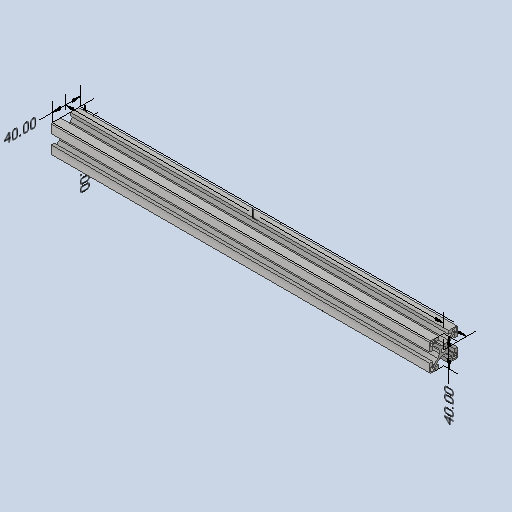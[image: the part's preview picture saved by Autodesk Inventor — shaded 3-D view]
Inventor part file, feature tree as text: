
AUTODESK INVENTOR PART (.ipt)
format: ipt  version: 2023 (Build 270158000, 158)  size: 276,480 bytes
history: native  units: mm
features: other x125, extrude x1, sketch x1
ambient origin geometry x8: Origin, YZ Plane, XZ Plane, XY Plane, X Axis, Y Axis, Z Axis, Center Point
bodies: Solid1 (feature_tree)
feature tree (127):
  other  "Annotations"
  extrude  "Extrusion1"  [1 undecoded]
  other  "CS_ANBAU_HINTEN_LINKS_XY"
  other  "CS_ANBAU_HINTEN_LINKS_YZ"
  other  "CS_ANBAU_HINTEN_LINKS_ZX"
  other  "CS_ANBAU_HINTEN_LINKS_X"
  other  "CS_ANBAU_HINTEN_LINKS_Y"
  other  "CS_ANBAU_HINTEN_LINKS_Z"
  other  "CS_ANBAU_HINTEN_LINKS_Center"
  other  "CS_ANBAU_HINTEN_OBEN_XY"
  other  "CS_ANBAU_HINTEN_OBEN_YZ"
  other  "CS_ANBAU_HINTEN_OBEN_ZX"
  other  "CS_ANBAU_HINTEN_OBEN_X"
  other  "CS_ANBAU_HINTEN_OBEN_Y"
  other  "CS_ANBAU_HINTEN_OBEN_Z"
  other  "CS_ANBAU_HINTEN_OBEN_Center"
  other  "CS_ANBAU_HINTEN_RECHTS_XY"
  other  "CS_ANBAU_HINTEN_RECHTS_YZ"
  other  "CS_ANBAU_HINTEN_RECHTS_ZX"
  other  "CS_ANBAU_HINTEN_RECHTS_X"
  other  "CS_ANBAU_HINTEN_RECHTS_Y"
  other  "CS_ANBAU_HINTEN_RECHTS_Z"
  other  "CS_ANBAU_HINTEN_RECHTS_Center"
  other  "CS_ANBAU_HINTEN_UNTEN_XY"
  other  "CS_ANBAU_HINTEN_UNTEN_YZ"
  other  "CS_ANBAU_HINTEN_UNTEN_ZX"
  other  "CS_ANBAU_HINTEN_UNTEN_X"
  other  "CS_ANBAU_HINTEN_UNTEN_Y"
  other  "CS_ANBAU_HINTEN_UNTEN_Z"
  other  "CS_ANBAU_HINTEN_UNTEN_Center"
  other  "CS_ANBAU_QUER_XY"
  other  "CS_ANBAU_QUER_YZ"
  other  "CS_ANBAU_QUER_ZX"
  other  "CS_ANBAU_QUER_X"
  other  "CS_ANBAU_QUER_Y"
  other  "CS_ANBAU_QUER_Z"
  other  "CS_ANBAU_QUER_Center"
  other  "CS_ANBAU_QUER_1_XY"
  other  "CS_ANBAU_QUER_1_YZ"
  other  "CS_ANBAU_QUER_1_ZX"
  other  "CS_ANBAU_QUER_1_X"
  other  "CS_ANBAU_QUER_1_Y"
  other  "CS_ANBAU_QUER_1_Z"
  other  "CS_ANBAU_QUER_1_Center"
  other  "CS_ANBAU_VORNE_LINKS_XY"
  other  "CS_ANBAU_VORNE_LINKS_YZ"
  other  "CS_ANBAU_VORNE_LINKS_ZX"
  other  "CS_ANBAU_VORNE_LINKS_X"
  other  "CS_ANBAU_VORNE_LINKS_Y"
  other  "CS_ANBAU_VORNE_LINKS_Z"
  other  "CS_ANBAU_VORNE_LINKS_Center"
  other  "CS_ANBAU_VORNE_OBEN_XY"
  other  "CS_ANBAU_VORNE_OBEN_YZ"
  other  "CS_ANBAU_VORNE_OBEN_ZX"
  other  "CS_ANBAU_VORNE_OBEN_X"
  other  "CS_ANBAU_VORNE_OBEN_Y"
  other  "CS_ANBAU_VORNE_OBEN_Z"
  other  "CS_ANBAU_VORNE_OBEN_Center"
  other  "CS_ANBAU_VORNE_RECHTS_XY"
  other  "CS_ANBAU_VORNE_RECHTS_YZ"
  other  "CS_ANBAU_VORNE_RECHTS_ZX"
  other  "CS_ANBAU_VORNE_RECHTS_X"
  other  "CS_ANBAU_VORNE_RECHTS_Y"
  other  "CS_ANBAU_VORNE_RECHTS_Z"
  other  "CS_ANBAU_VORNE_RECHTS_Center"
  other  "CS_ANBAU_VORNE_UNTEN_XY"
  other  "CS_ANBAU_VORNE_UNTEN_YZ"
  other  "CS_ANBAU_VORNE_UNTEN_ZX"
  other  "CS_ANBAU_VORNE_UNTEN_X"
  other  "CS_ANBAU_VORNE_UNTEN_Y"
  other  "CS_ANBAU_VORNE_UNTEN_Z"
  other  "CS_ANBAU_VORNE_UNTEN_Center"
  other  "p1_XY"
  other  "p1_YZ"
  other  "p1_ZX"
  other  "p1_X"
  other  "p1_Y"
  other  "p1_Z"
  other  "p1_Center"
  other  "p2_XY"
  other  "p2_YZ"
  other  "p2_ZX"
  other  "p2_X"
  other  "p2_Y"
  other  "p2_Z"
  other  "p2_Center"
  other  "p3_XY"
  other  "p3_YZ"
  other  "p3_ZX"
  other  "p3_X"
  other  "p3_Y"
  other  "p3_Z"
  other  "p3_Center"
  other  "p4_XY"
  other  "p4_YZ"
  other  "p4_ZX"
  other  "p4_X"
  other  "p4_Y"
  other  "p4_Z"
  other  "p4_Center"
  other  "p5_XY"
  other  "p5_YZ"
  other  "p5_ZX"
  other  "p5_X"
  other  "p5_Y"
  other  "p5_Z"
  other  "p5_Center"
  other  "pm1_XY"
  other  "pm1_YZ"
  other  "pm1_ZX"
  other  "pm1_X"
  other  "pm1_Y"
  other  "pm1_Z"
  other  "pm1_Center"
  other  "pm2_XY"
  other  "pm2_YZ"
  other  "pm2_ZX"
  other  "pm2_X"
  other  "pm2_Y"
  other  "pm2_Z"
  other  "pm2_Center"
  sketch  "Skizze_1"  dims[d0=540.0mm d1=0.0mm d2=0.0mm d3=0.0mm d4=0.0mm d5=0.0mm d6=0.0mm d10=540.0mm d11=540.0mm d7=40.0mm d8=40.0mm d9=40.0mm]
  other  "Linear Dimension 1"
  other  "Linear Dimension 2"
  other  "Linear Dimension 3"
  other  "Linear Dimension 4"
  other  "Linear Dimension 5"
note: 1 required parameter value undecoded (feature->parameter linkage not recoverable at this tier; creation-order binding heuristic only, values carry confidence <= 0.55)
